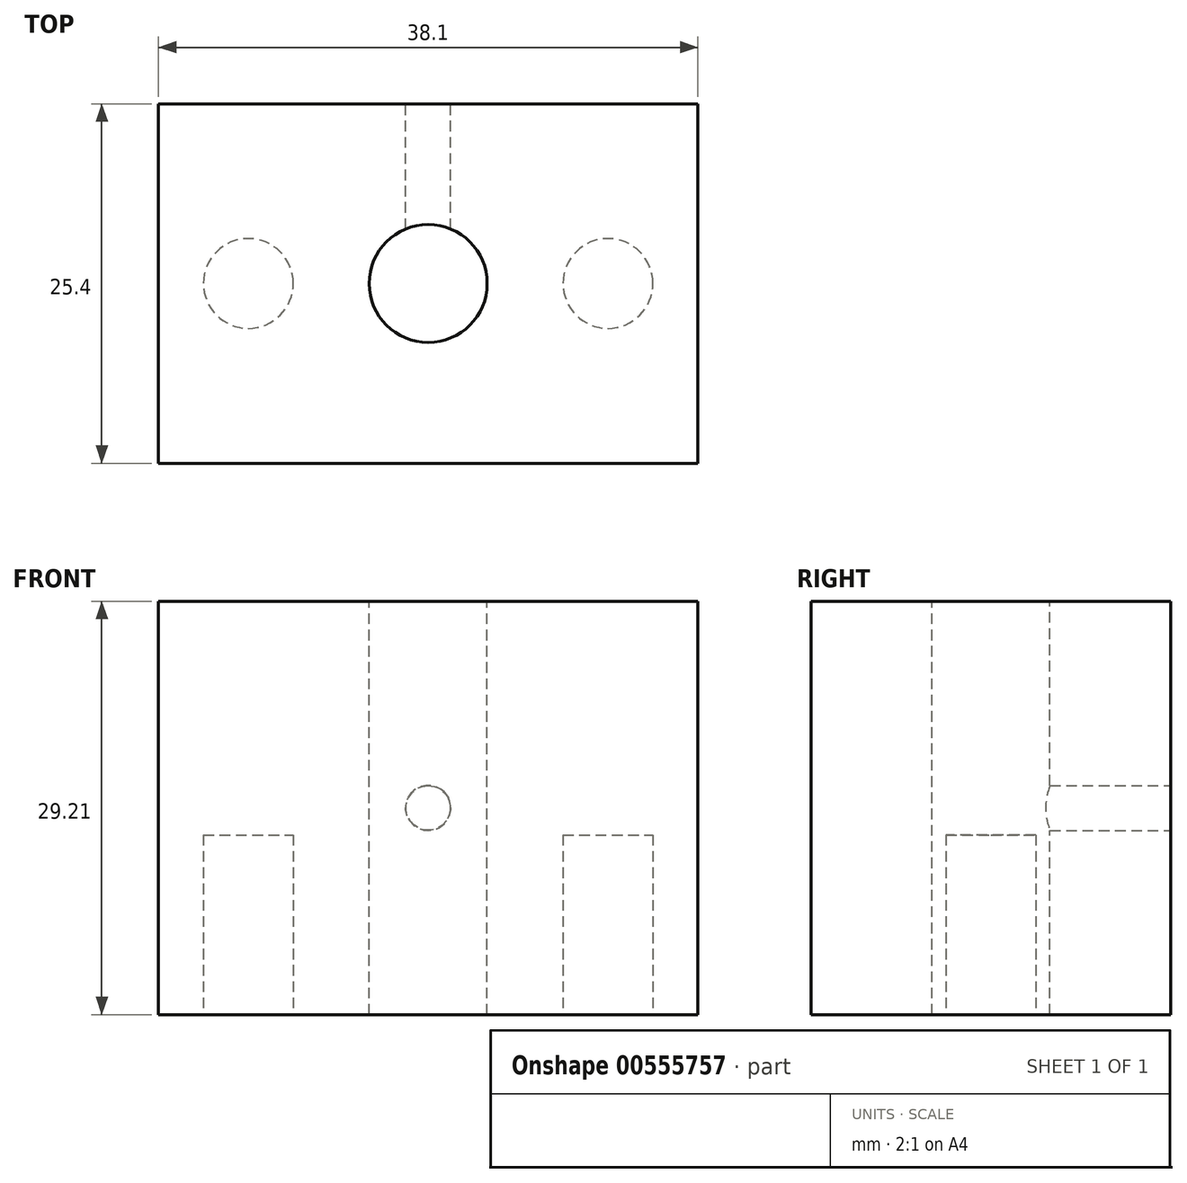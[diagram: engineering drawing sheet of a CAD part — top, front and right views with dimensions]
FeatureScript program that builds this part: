
annotation { "Feature Type Name" : "Feature", "Feature Type Description" : "" }
export const myFeature = defineFeature(function(context is Context, id is Id, definition is map)
    precondition{}
    {
        {
            var Q0;
            Q0=qCreatedBy(makeId("Top.planeOp"),FACE);
            var sketch = newSketch(context, id + "F0", { "sketchPlane" : qUnion([Q0])});
            skLineSegment(sketch, "E0.bottom", {"start": v(19.05, -12.7) * mm, "end": v(-19.05, -12.7) * mm});
            skLineSegment(sketch, "E0.top", {"start": v(19.05, 12.7) * mm, "end": v(-19.05, 12.7) * mm});
            skLineSegment(sketch, "E0.left", {"start": v(19.05, -12.7) * mm, "end": v(19.05, 12.7) * mm});
            skLineSegment(sketch, "E0.right", {"start": v(-19.05, -12.7) * mm, "end": v(-19.05, 12.7) * mm});
            skPoint(sketch, "E0.middle", {"position": v(0, 0) * mm});
            skCircle(sketch, "E1", {"center": v(0, 0) * mm, "radius": 4.17 * mm});
            skSolve(sketch);
        }
        {
            var Q0;
            Q0=makeQuery(id+"F0.imprint","IMPRINT",FACE,{"disambiguationData":[TD([[makeQuery(id+"F0.imprint","IMPRINT",EDGE,{"derivedFrom":sQuery(id+"F0.wireOp",EDGE,"E0.bottom")}),-1.0]])]});
            extrude(context, id + "F1", {"entities" : qUnion([Q0]), "oppositeDirection" : true, "depth" : 29.2 * mm, "offsetDistance" : 25.4 * mm});
        }
        {
            var Q0;
            Q0=makeQuery(id+"F1.opExtrude","CAP_FACE",FACE,{"disambiguationData":[OSD([sQuery(id+"F0.wireOp",EDGE,"E0.bottom"),sQuery(id+"F0.wireOp",EDGE,"E0.top"),sQuery(id+"F0.wireOp",EDGE,"E0.left"),sQuery(id+"F0.wireOp",EDGE,"E0.right"),sQuery(id+"F0.wireOp",EDGE,"E1")])],"isStart":false});
            var sketch = newSketch(context, id + "F2", { "sketchPlane" : qUnion([Q0])});
            skCircle(sketch, "E2", {"center": v(-12.7, 0) * mm, "radius": 3.18 * mm});
            skCircle(sketch, "E3", {"center": v(12.7, 0) * mm, "radius": 3.18 * mm});
            skSolve(sketch);
        }
        {
            var Q0;
            Q0=makeQuery(id+"F2.imprint","IMPRINT",FACE,{"disambiguationData":[TD([[makeQuery(id+"F2.imprint","IMPRINT",EDGE,{"derivedFrom":sQuery(id+"F2.wireOp",EDGE,"E2")}),1.0]])]});
            var Q1;
            Q1=makeQuery(id+"F2.imprint","IMPRINT",FACE,{"disambiguationData":[TD([[makeQuery(id+"F2.imprint","IMPRINT",EDGE,{"derivedFrom":sQuery(id+"F2.wireOp",EDGE,"E3")}),1.0]])]});
            extrude(context, id + "F3", {"entities" : qUnion([Q0, Q1]), "operationType" : NewBodyOperationType.REMOVE, "oppositeDirection" : true, "depth" : 12.7 * mm, "offsetDistance" : 25.4 * mm});
        }
        {
            var Q0;
            Q0=makeQuery(id+"F1.opExtrude","SWEPT_FACE",FACE,{"disambiguationData":[OSD([sQuery(id+"F0.wireOp",EDGE,"E0.top")])]});
            var sketch = newSketch(context, id + "F4", { "sketchPlane" : qUnion([Q0])});
            skCircle(sketch, "E4", {"center": v(0, -14.6) * mm, "radius": 1.59 * mm});
            skSolve(sketch);
        }
        {
            var Q0;
            Q0 = qSketchRegion(id + "F4", true);
            extrude(context, id + "F5", {"entities" : qUnion([Q0]), "operationType" : NewBodyOperationType.REMOVE, "oppositeDirection" : true, "depth" : 12.7 * mm, "offsetDistance" : 25.4 * mm});
        }
    });
